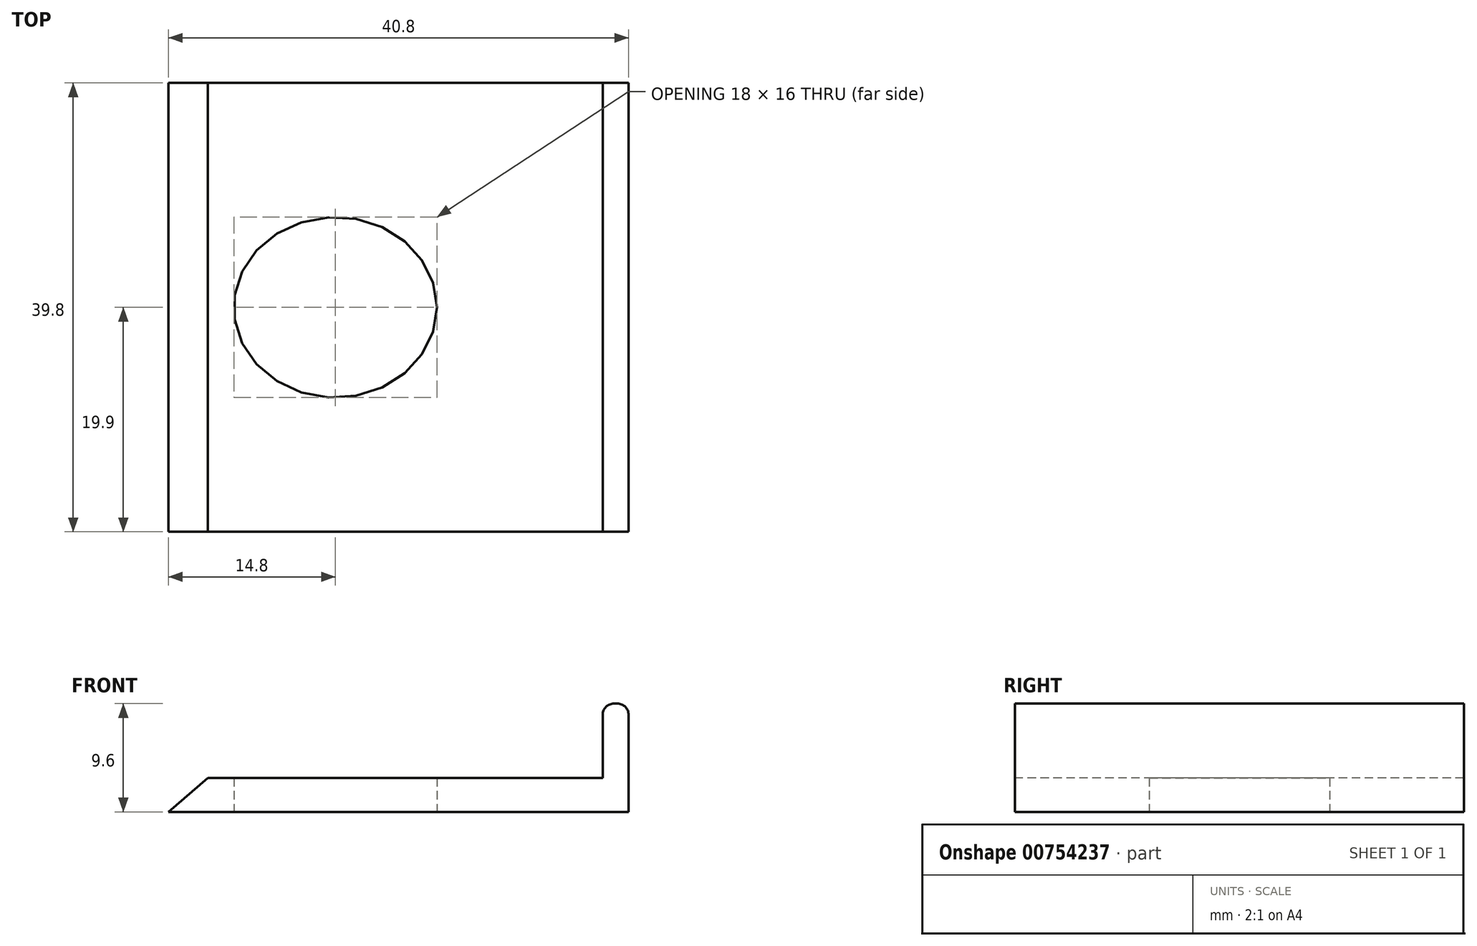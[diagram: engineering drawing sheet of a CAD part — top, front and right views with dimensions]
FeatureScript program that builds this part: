
annotation { "Feature Type Name" : "Feature", "Feature Type Description" : "" }
export const myFeature = defineFeature(function(context is Context, id is Id, definition is map)
    precondition{}
    {
        {
            var Q0;
            Q0=qCreatedBy(makeId("Top.planeOp"),FACE);
            var sketch = newSketch(context, id + "F0", { "sketchPlane" : qUnion([Q0])});
            skLineSegment(sketch, "E0.bottom", {"start": v(-20.4, 19.9) * mm, "end": v(20.4, 19.9) * mm});
            skLineSegment(sketch, "E0.top", {"start": v(-20.4, -19.9) * mm, "end": v(20.4, -19.9) * mm});
            skLineSegment(sketch, "E0.left", {"start": v(-20.4, 19.9) * mm, "end": v(-20.4, -19.9) * mm});
            skLineSegment(sketch, "E0.right", {"start": v(20.4, 19.9) * mm, "end": v(20.4, -19.9) * mm});
            skLineSegment(sketch, "E1", {"start": v(18.1, 19.9) * mm, "end": v(18.1, -19.9) * mm});
            skEllipse(sketch, "E2", {"center": v(-5.6, 0) * mm, "majorRadius": 9 * mm, "minorRadius": 8 * mm, "majorAxis": v(1, 0)});
            skSolve(sketch);
        }
        {
            var Q0;
            Q0 = qSketchRegion(id + "F0", true);
            extrude(context, id + "F1", {"entities" : qUnion([Q0]), "depth" : 3 * mm, "offsetDistance" : 25 * mm});
        }
        {
            var Q0;
            {var subQ0=sQuery(id+"F0.wireOp",EDGE,"E0.right");Q0=makeQuery(id+"F0.imprint","IMPRINT",FACE,{"disambiguationData":[TD([[makeQuery(id+"F0.imprint","IMPRINT",EDGE,{"derivedFrom":subQ0}),-1.0]])]});}
            extrude(context, id + "F2", {"entities" : qUnion([Q0]), "operationType" : NewBodyOperationType.ADD, "depth" : 9.6 * mm, "offsetDistance" : 25 * mm});
        }
        {
            var Q0;
            Q0=makeQuery(id+"F2.opExtrude","CAP_EDGE",EDGE,{"disambiguationData":[OSD([sQuery(id+"F0.wireOp",EDGE,"E1")])],"isStart":false});
            var Q1;
            Q1=makeQuery(id+"F2.opExtrude","CAP_EDGE",EDGE,{"disambiguationData":[OSD([sQuery(id+"F0.wireOp",EDGE,"E0.right")])],"isStart":false});
            fillet(context, id + "F3", {"entities" : qUnion([Q0, Q1]), "radius" : 1 * mm, "tangentPropagation" : true, "allowEdgeOverflow" : false});
        }
        {
            var Q0;
            Q0=makeQuery(id+"F1.opExtrude","CAP_EDGE",EDGE,{"disambiguationData":[OSD([sQuery(id+"F0.wireOp",EDGE,"E0.left")])],"isStart":false});
            chamfer(context, id + "F4", {"entities" : qUnion([Q0]), "chamferType" : ChamferType.TWO_OFFSETS, "width1" : 3.5 * mm, "oppositeDirection" : false, "width2" : 3 * mm, "tangentPropagation" : true});
        }
    });
